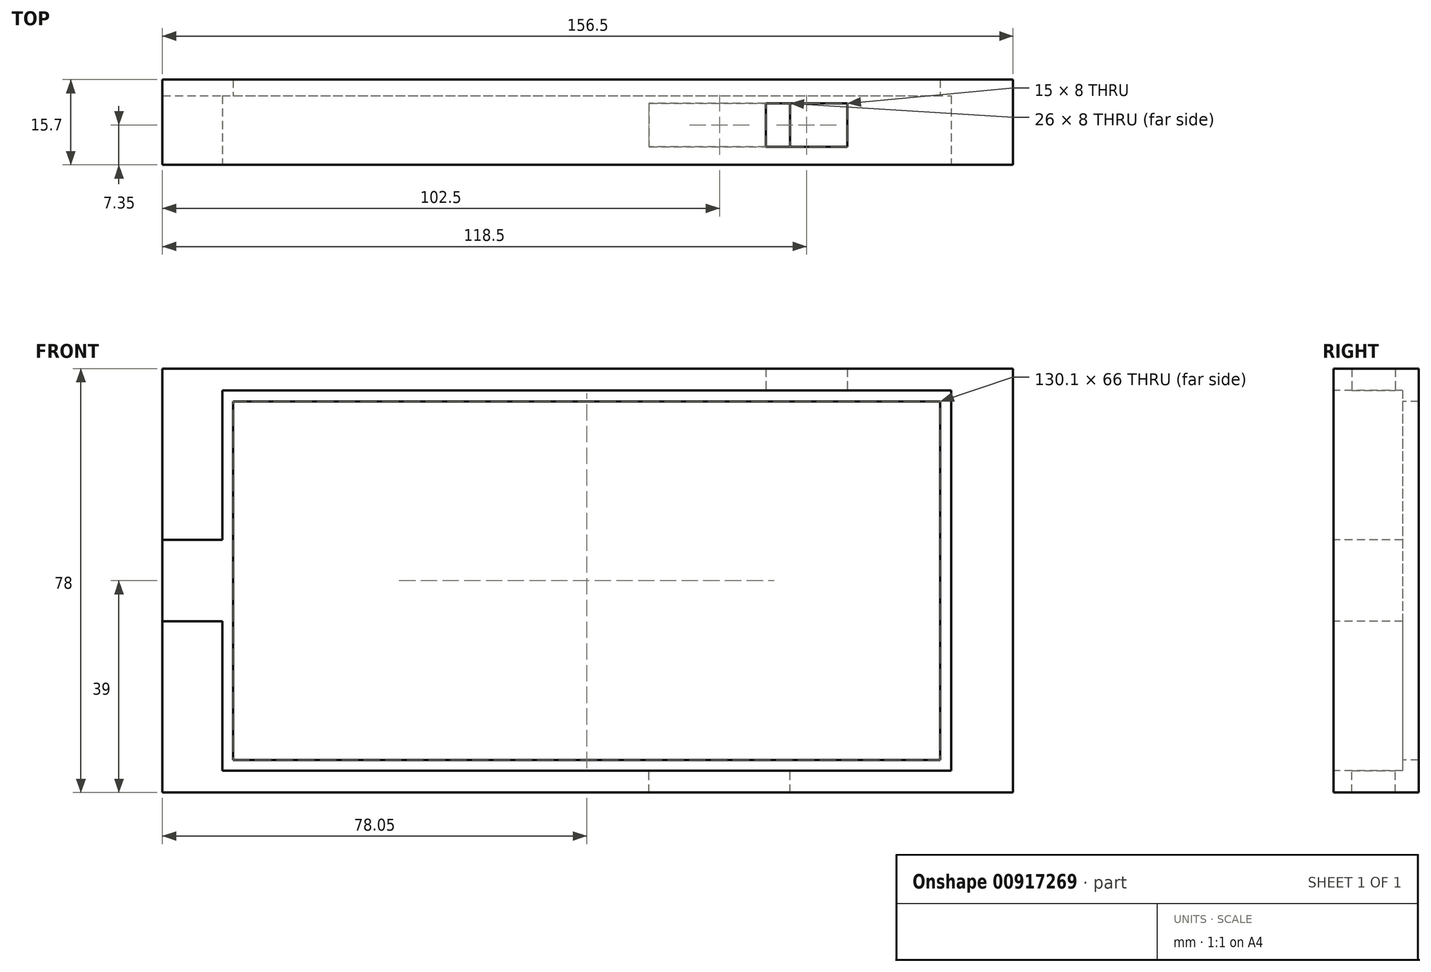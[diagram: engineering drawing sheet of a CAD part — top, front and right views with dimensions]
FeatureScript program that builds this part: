
annotation { "Feature Type Name" : "Feature", "Feature Type Description" : "" }
export const myFeature = defineFeature(function(context is Context, id is Id, definition is map)
    precondition{}
    {
        {
            var Q0;
            Q0=qCreatedBy(makeId("Front.planeOp"),FACE);
            var sketch = newSketch(context, id + "F0", { "sketchPlane" : qUnion([Q0])});
            skLineSegment(sketch, "E0.bottom", {"start": v(-67.25, 35) * mm, "end": v(67.25, 35) * mm});
            skLineSegment(sketch, "E0.top", {"start": v(-67.25, -35) * mm, "end": v(67.25, -35) * mm});
            skLineSegment(sketch, "E0.left", {"start": v(-67.25, 35) * mm, "end": v(-67.25, -35) * mm});
            skLineSegment(sketch, "E0.right", {"start": v(67.25, 35) * mm, "end": v(67.25, -35) * mm});
            skPoint(sketch, "E0.middle", {"position": v(0, 0) * mm});
            skLineSegment(sketch, "E1.0", {"start": v(-71.25, 39) * mm, "end": v(71.25, 39) * mm});
            skLineSegment(sketch, "E1.1", {"start": v(-71.25, 39) * mm, "end": v(-71.25, -39) * mm});
            skLineSegment(sketch, "E1.2", {"start": v(-71.25, -39) * mm, "end": v(71.25, -39) * mm});
            skLineSegment(sketch, "E1.3", {"start": v(71.25, 39) * mm, "end": v(71.25, -39) * mm});
            skLineSegment(sketch, "E2.bottom", {"start": v(-67.25, 35) * mm, "end": v(-65.25, 35) * mm});
            skLineSegment(sketch, "E2.top", {"start": v(-67.25, -35) * mm, "end": v(-65.25, -35) * mm});
            skLineSegment(sketch, "E2.right", {"start": v(-65.25, 35) * mm, "end": v(-65.25, -35) * mm});
            skLineSegment(sketch, "E3.bottom", {"start": v(67.25, 35) * mm, "end": v(65.25, 35) * mm});
            skLineSegment(sketch, "E3.top", {"start": v(67.25, -35) * mm, "end": v(65.25, -35) * mm});
            skLineSegment(sketch, "E3.right", {"start": v(65.25, 35) * mm, "end": v(65.25, -35) * mm});
            skLineSegment(sketch, "E4.bottom", {"start": v(-65.25, 35) * mm, "end": v(65.25, 35) * mm});
            skLineSegment(sketch, "E4.top", {"start": v(-65.25, 33) * mm, "end": v(65.25, 33) * mm});
            skLineSegment(sketch, "E4.left", {"start": v(-65.25, 35) * mm, "end": v(-65.25, 33) * mm});
            skLineSegment(sketch, "E4.right", {"start": v(65.25, 35) * mm, "end": v(65.25, 33) * mm});
            skLineSegment(sketch, "E5.bottom", {"start": v(-65.25, -35) * mm, "end": v(65.25, -35) * mm});
            skLineSegment(sketch, "E5.top", {"start": v(-65.25, -33) * mm, "end": v(65.25, -33) * mm});
            skLineSegment(sketch, "E5.left", {"start": v(-65.25, -35) * mm, "end": v(-65.25, -33) * mm});
            skLineSegment(sketch, "E5.right", {"start": v(65.25, -35) * mm, "end": v(65.25, -33) * mm});
            skLineSegment(sketch, "E6.bottom", {"start": v(-71.25, 39) * mm, "end": v(-78.25, 39) * mm});
            skLineSegment(sketch, "E6.top", {"start": v(-71.25, -39) * mm, "end": v(-78.25, -39) * mm});
            skLineSegment(sketch, "E6.right", {"start": v(-78.25, 39) * mm, "end": v(-78.25, -39) * mm});
            skLineSegment(sketch, "E7.bottom", {"start": v(71.25, 39) * mm, "end": v(78.25, 39) * mm});
            skLineSegment(sketch, "E7.top", {"start": v(71.25, -39) * mm, "end": v(78.25, -39) * mm});
            skLineSegment(sketch, "E7.right", {"start": v(78.25, 39) * mm, "end": v(78.25, -39) * mm});
            skSolve(sketch);
        }
        {
            var Q0;
            {var subQ3=sQuery(id+"F0.wireOp",EDGE,"E0.right");Q0=makeQuery(id+"F0.imprint","IMPRINT",FACE,{"disambiguationData":[TD([[makeQuery(id+"F0.imprint","IMPRINT",EDGE,{"derivedFrom":subQ3}),-1.0]])]});}
            var Q1;
            {var subQ5=sQuery(id+"F0.wireOp",EDGE,"E4.top");Q1=makeQuery(id+"F0.imprint","IMPRINT",FACE,{"disambiguationData":[TD([[makeQuery(id+"F0.imprint","IMPRINT",EDGE,{"derivedFrom":subQ5}),1.0]])]});}
            var Q2;
            {var subQ5=sQuery(id+"F0.wireOp",EDGE,"E0.left");Q2=makeQuery(id+"F0.imprint","IMPRINT",FACE,{"disambiguationData":[TD([[makeQuery(id+"F0.imprint","IMPRINT",EDGE,{"derivedFrom":subQ5}),1.0]])]});}
            var Q3;
            {var subQ5=sQuery(id+"F0.wireOp",EDGE,"E5.top");Q3=makeQuery(id+"F0.imprint","IMPRINT",FACE,{"disambiguationData":[TD([[makeQuery(id+"F0.imprint","IMPRINT",EDGE,{"derivedFrom":subQ5}),-1.0]])]});}
            extrude(context, id + "F1", {"entities" : qUnion([Q0, Q1, Q2, Q3]), "oppositeDirection" : true, "depth" : 3 * mm, "offsetDistance" : 25 * mm});
        }
        {
            var Q0;
            {var subQ1=sQuery(id+"F0.wireOp",EDGE,"E0.left");Q0=makeQuery(id+"F0.imprint","IMPRINT",FACE,{"disambiguationData":[TD([[makeQuery(id+"F0.imprint","IMPRINT",EDGE,{"derivedFrom":subQ1}),-1.0]])]});}
            var Q1;
            Q1=makeQuery(id+"F0.imprint","IMPRINT",FACE,{"disambiguationData":[TD([[makeQuery(id+"F0.imprint","IMPRINT",EDGE,{"derivedFrom":sQuery(id+"F0.wireOp",EDGE,"E1.1")}),-1.0]])]});
            var Q2;
            Q2=makeQuery(id+"F0.imprint","IMPRINT",FACE,{"disambiguationData":[TD([[makeQuery(id+"F0.imprint","IMPRINT",EDGE,{"derivedFrom":sQuery(id+"F0.wireOp",EDGE,"E1.3")}),1.0]])]});
            extrude(context, id + "F2", {"entities" : qUnion([Q0, Q1, Q2]), "operationType" : NewBodyOperationType.ADD, "oppositeDirection" : true, "depth" : 3 * mm, "offsetDistance" : 25 * mm, "hasSecondDirection" : true, "secondDirectionOppositeDirection" : false, "secondDirectionDepth" : 12.7 * mm});
        }
        {
            var Q0;
            Q0=makeQuery(id+"F2.opExtrude","CAP_FACE",FACE,{"disambiguationData":[OSD([sQuery(id+"F0.wireOp",EDGE,"E0.bottom"),sQuery(id+"F0.wireOp",EDGE,"E0.top"),sQuery(id+"F0.wireOp",EDGE,"E0.left"),sQuery(id+"F0.wireOp",EDGE,"E0.right"),sQuery(id+"F0.wireOp",EDGE,"E1.0"),sQuery(id+"F0.wireOp",EDGE,"E1.2"),sQuery(id+"F0.wireOp",EDGE,"E6.bottom"),sQuery(id+"F0.wireOp",EDGE,"E6.top"),sQuery(id+"F0.wireOp",EDGE,"E6.right"),sQuery(id+"F0.wireOp",EDGE,"E7.bottom"),sQuery(id+"F0.wireOp",EDGE,"E7.top"),sQuery(id+"F0.wireOp",EDGE,"E7.right")])],"isStart":true});
            var sketch = newSketch(context, id + "F3", { "sketchPlane" : qUnion([Q0])});
            skLineSegment(sketch, "E8", {"start": v(-67.25, 0) * mm, "end": v(-78.25, 0) * mm});
            skLineSegment(sketch, "E9", {"start": v(-72.75, 0) * mm, "end": v(-72.75, 39) * mm});
            skLineSegment(sketch, "E10", {"start": v(-72.75, 0) * mm, "end": v(-72.75, -39) * mm});
            skLineSegment(sketch, "E11.bottom", {"start": v(-78.25, 7.5) * mm, "end": v(-67.25, 7.5) * mm});
            skLineSegment(sketch, "E11.top", {"start": v(-78.25, -7.5) * mm, "end": v(-67.25, -7.5) * mm});
            skLineSegment(sketch, "E11.left", {"start": v(-78.25, 7.5) * mm, "end": v(-78.25, -7.5) * mm});
            skLineSegment(sketch, "E11.right", {"start": v(-67.25, 7.5) * mm, "end": v(-67.25, -7.5) * mm});
            skPoint(sketch, "E11.middle", {"position": v(-72.75, 0) * mm});
            skSolve(sketch);
        }
        {
            var Q0;
            {var subQ0=sQuery(id+"F3.wireOp",EDGE,"E11.left");var subQ1=sQuery(id+"F3.wireOp",EDGE,"E8");var subQ2=makeQuery(id+"F3.imprint","INTERSECT",VERTEX,{"derivedFrom":[subQ1,subQ0]});Q0=makeQuery(id+"F3.imprint","IMPRINT",FACE,{"disambiguationData":[TD([[makeQuery(id+"F3.imprint","IMPRINT",EDGE,{"disambiguationData":[TD([[subQ2,1.0]])],"derivedFrom":subQ1}),-1.0]])]});}
            var Q1;
            {var subQ0=sQuery(id+"F3.wireOp",EDGE,"E11.right");var subQ1=sQuery(id+"F3.wireOp",EDGE,"E8");var subQ2=makeQuery(id+"F3.imprint","INTERSECT",VERTEX,{"derivedFrom":[subQ1,subQ0]});Q1=makeQuery(id+"F3.imprint","IMPRINT",FACE,{"disambiguationData":[TD([[makeQuery(id+"F3.imprint","IMPRINT",EDGE,{"disambiguationData":[TD([[subQ2,-1.0]])],"derivedFrom":subQ1}),-1.0]])]});}
            var Q2;
            {var subQ0=sQuery(id+"F3.wireOp",EDGE,"E11.right");var subQ1=sQuery(id+"F3.wireOp",EDGE,"E8");var subQ2=makeQuery(id+"F3.imprint","INTERSECT",VERTEX,{"derivedFrom":[subQ1,subQ0]});Q2=makeQuery(id+"F3.imprint","IMPRINT",FACE,{"disambiguationData":[TD([[makeQuery(id+"F3.imprint","IMPRINT",EDGE,{"disambiguationData":[TD([[subQ2,-1.0]])],"derivedFrom":subQ1}),1.0]])]});}
            var Q3;
            {var subQ0=sQuery(id+"F3.wireOp",EDGE,"E11.left");var subQ1=sQuery(id+"F3.wireOp",EDGE,"E8");var subQ2=makeQuery(id+"F3.imprint","INTERSECT",VERTEX,{"derivedFrom":[subQ1,subQ0]});Q3=makeQuery(id+"F3.imprint","IMPRINT",FACE,{"disambiguationData":[TD([[makeQuery(id+"F3.imprint","IMPRINT",EDGE,{"disambiguationData":[TD([[subQ2,1.0]])],"derivedFrom":subQ1}),1.0]])]});}
            extrude(context, id + "F4", {"entities" : qUnion([Q0, Q1, Q2, Q3]), "operationType" : NewBodyOperationType.REMOVE, "oppositeDirection" : true, "depth" : 12.7 * mm, "offsetDistance" : 25 * mm});
        }
        {
            var Q0;
            Q0=makeQuery(id+"F2.opExtrude","SWEPT_FACE",FACE,{"disambiguationData":[OSD([sQuery(id+"F0.wireOp",EDGE,"E0.bottom")])]});
            var sketch = newSketch(context, id + "F5", { "sketchPlane" : qUnion([Q0])});
            skLineSegment(sketch, "E12", {"start": v(67.25, 6.35) * mm, "end": v(40.25, 6.35) * mm});
            skLineSegment(sketch, "E13.bottom", {"start": v(47.75, 9.35) * mm, "end": v(32.75, 9.35) * mm});
            skLineSegment(sketch, "E13.top", {"start": v(47.75, 3.35) * mm, "end": v(32.75, 3.35) * mm});
            skLineSegment(sketch, "E13.left", {"start": v(47.75, 9.35) * mm, "end": v(47.75, 3.35) * mm});
            skLineSegment(sketch, "E13.right", {"start": v(32.75, 9.35) * mm, "end": v(32.75, 3.35) * mm});
            skPoint(sketch, "E13.middle", {"position": v(40.25, 6.35) * mm});
            skSolve(sketch);
        }
        {
            var Q0;
            {var subQ3=sQuery(id+"F5.wireOp",EDGE,"E13.bottom");Q0=makeQuery(id+"F5.imprint","IMPRINT",FACE,{"disambiguationData":[TD([[makeQuery(id+"F5.imprint","IMPRINT",EDGE,{"derivedFrom":subQ3}),1.0]])]});}
            extrude(context, id + "F6", {"entities" : qUnion([Q0]), "operationType" : NewBodyOperationType.REMOVE, "endBound" : BoundingType.THROUGH_ALL, "oppositeDirection" : true, "depth" : 25 * mm, "offsetDistance" : 25 * mm});
        }
        {
            var Q0;
            Q0=makeQuery(id+"F2.opExtrude","SWEPT_FACE",FACE,{"disambiguationData":[OSD([sQuery(id+"F0.wireOp",EDGE,"E0.top")])]});
            var sketch = newSketch(context, id + "F7", { "sketchPlane" : qUnion([Q0])});
            skLineSegment(sketch, "E14", {"start": v(67.25, -6.35) * mm, "end": v(24.25, -6.35) * mm});
            skLineSegment(sketch, "E15.bottom", {"start": v(37.25, -9.35) * mm, "end": v(11.25, -9.35) * mm});
            skLineSegment(sketch, "E15.top", {"start": v(37.25, -3.35) * mm, "end": v(11.25, -3.35) * mm});
            skLineSegment(sketch, "E15.left", {"start": v(37.25, -9.35) * mm, "end": v(37.25, -3.35) * mm});
            skLineSegment(sketch, "E15.right", {"start": v(11.25, -9.35) * mm, "end": v(11.25, -3.35) * mm});
            skPoint(sketch, "E15.middle", {"position": v(24.25, -6.35) * mm});
            skSolve(sketch);
        }
        {
            var Q0;
            {var subQ3=sQuery(id+"F7.wireOp",EDGE,"E15.bottom");Q0=makeQuery(id+"F7.imprint","IMPRINT",FACE,{"disambiguationData":[TD([[makeQuery(id+"F7.imprint","IMPRINT",EDGE,{"derivedFrom":subQ3}),-1.0]])]});}
            extrude(context, id + "F8", {"entities" : qUnion([Q0]), "operationType" : NewBodyOperationType.REMOVE, "endBound" : BoundingType.THROUGH_ALL, "oppositeDirection" : true, "depth" : 25 * mm, "offsetDistance" : 25 * mm});
        }
        {
            var Q0;
            Q0=makeQuery(id+"F2.opExtrude","SWEPT_FACE",FACE,{"disambiguationData":[OSD([sQuery(id+"F0.wireOp",EDGE,"E0.right")])]});
            var Q1;
            Q1=makeQuery(id+"F1.opExtrude","SWEPT_FACE",FACE,{"disambiguationData":[OSD([sQuery(id+"F0.wireOp",EDGE,"E3.right")])]});
            extrude(context, id + "F9", {"entities" : qUnion([Q0, Q1]), "operationType" : NewBodyOperationType.ADD, "depth" : 0.4 * mm, "offsetDistance" : 25 * mm});
        }
        {
            var Q0;
            Q0=makeQuery(id+"F8.boolean.opBoolean","COPY",FACE,{"derivedFrom":makeQuery(id+"F8.opExtrude","SWEPT_FACE",FACE,{"disambiguationData":[OSD([sQuery(id+"F7.wireOp",EDGE,"E15.top")])]})});
            extrude(context, id + "F10", {"entities" : qUnion([Q0]), "operationType" : NewBodyOperationType.REMOVE, "oppositeDirection" : true, "depth" : 2 * mm, "offsetDistance" : 25 * mm});
        }
        {
            var Q0;
            Q0=makeQuery(id+"F6.boolean.opBoolean","COPY",FACE,{"derivedFrom":makeQuery(id+"F6.opExtrude","SWEPT_FACE",FACE,{"disambiguationData":[OSD([sQuery(id+"F5.wireOp",EDGE,"E13.top")])]})});
            extrude(context, id + "F11", {"entities" : qUnion([Q0]), "operationType" : NewBodyOperationType.REMOVE, "oppositeDirection" : true, "depth" : 2 * mm, "offsetDistance" : 25 * mm});
        }
    });
